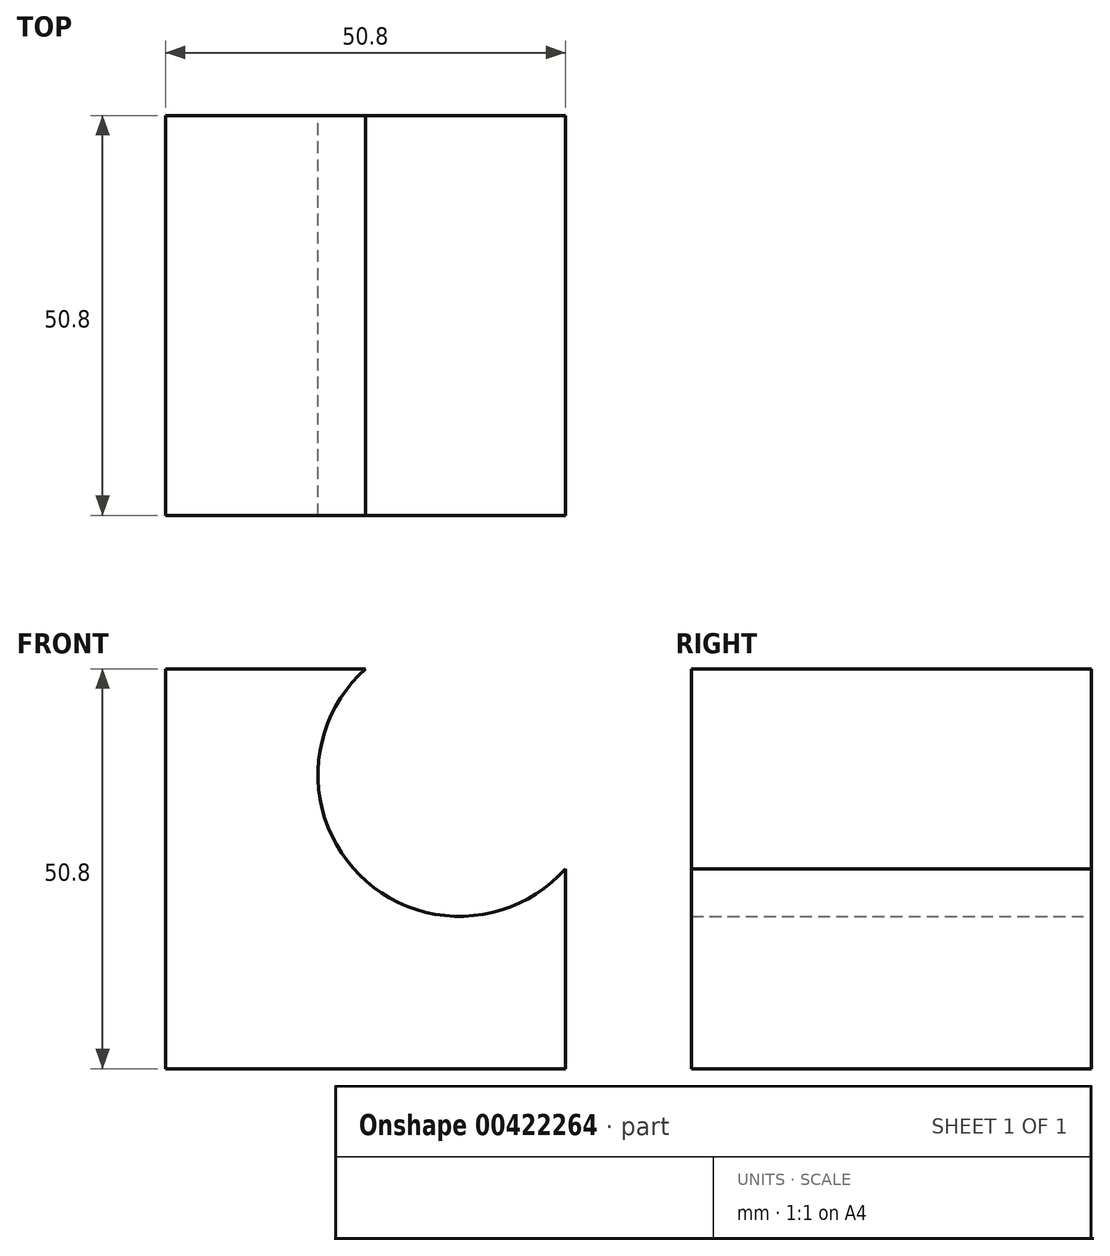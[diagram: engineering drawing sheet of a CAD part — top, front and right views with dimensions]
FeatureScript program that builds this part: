
annotation { "Feature Type Name" : "Feature", "Feature Type Description" : "" }
export const myFeature = defineFeature(function(context is Context, id is Id, definition is map)
    precondition{}
    {
        {
            var Q0;
            Q0=qCreatedBy(makeId("Front.planeOp"),FACE);
            var sketch = newSketch(context, id + "F0", { "sketchPlane" : qUnion([Q0])});
            skLineSegment(sketch, "E0", {"start": v(0, 0) * mm, "end": v(-50.8, 0) * mm});
            skLineSegment(sketch, "E1", {"start": v(-50.8, 0) * mm, "end": v(-50.8, 50.8) * mm});
            skLineSegment(sketch, "E2", {"start": v(-50.8, 50.8) * mm, "end": v(-25.4, 50.8) * mm});
            skLineSegment(sketch, "E3", {"start": v(0, 0) * mm, "end": v(0, 25.4) * mm});
            skArc(sketch, "E4", {"start": v(-25.4, 50.8) * mm, "mid": v(-26.18, 24.62) * mm, "end": v(0, 25.4) * mm});
            skSolve(sketch);
        }
        {
            var Q0;
            Q0=makeQuery(id+"F0.imprint","IMPRINT",FACE,{"disambiguationData":[TD([[makeQuery(id+"F0.imprint","IMPRINT",EDGE,{"derivedFrom":sQuery(id+"F0.wireOp",EDGE,"E0")}),-1.0]])]});
            extrude(context, id + "F1", {"entities" : qUnion([Q0]), "depth" : 50.8 * mm});
        }
    });
